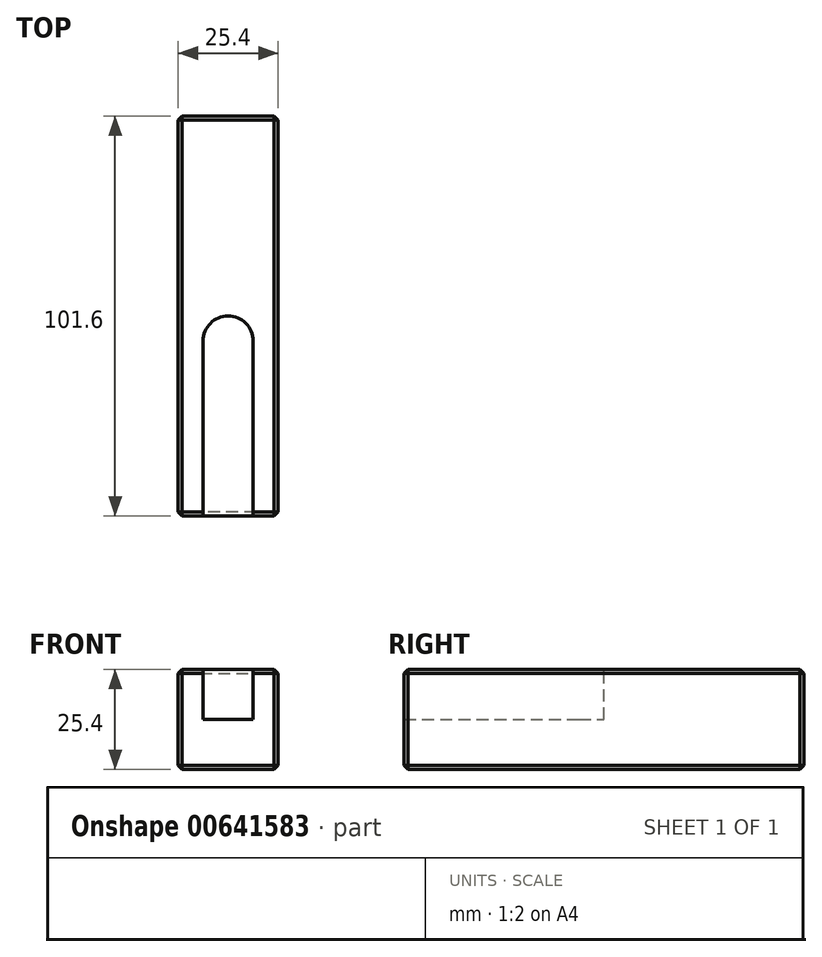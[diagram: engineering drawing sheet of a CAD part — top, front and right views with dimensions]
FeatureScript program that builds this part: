
annotation { "Feature Type Name" : "Feature", "Feature Type Description" : "" }
export const myFeature = defineFeature(function(context is Context, id is Id, definition is map)
    precondition{}
    {
        {
            var Q0;
            Q0=qCreatedBy(makeId("Front.planeOp"),FACE);
            var sketch = newSketch(context, id + "F0", { "sketchPlane" : qUnion([Q0])});
            skLineSegment(sketch, "E0.bottom", {"start": v(12.7, -12.7) * mm, "end": v(-12.7, -12.7) * mm});
            skLineSegment(sketch, "E0.top", {"start": v(12.7, 12.7) * mm, "end": v(-12.7, 12.7) * mm});
            skLineSegment(sketch, "E0.left", {"start": v(12.7, -12.7) * mm, "end": v(12.7, 12.7) * mm});
            skLineSegment(sketch, "E0.right", {"start": v(-12.7, -12.7) * mm, "end": v(-12.7, 12.7) * mm});
            skPoint(sketch, "E0.middle", {"position": v(0, 0) * mm});
            skSolve(sketch);
        }
        {
            var Q0;
            Q0=makeQuery(id+"F0.imprint","IMPRINT",FACE,{"disambiguationData":[TD([[makeQuery(id+"F0.imprint","IMPRINT",EDGE,{"derivedFrom":sQuery(id+"F0.wireOp",EDGE,"E0.bottom")}),-1.0]])]});
            extrude(context, id + "F1", {"entities" : qUnion([Q0]), "endBound" : BoundingType.SYMMETRIC, "oppositeDirection" : true, "depth" : (25.4 * 4) * mm, "offsetDistance" : 25 * mm});
        }
        {
            var Q0;
            Q0=makeQuery(id+"F1.opExtrude","SWEPT_FACE",FACE,{"disambiguationData":[OSD([sQuery(id+"F0.wireOp",EDGE,"E0.top")])]});
            var sketch = newSketch(context, id + "F2", { "sketchPlane" : qUnion([Q0])});
            skLineSegment(sketch, "E1.bottom", {"start": v(-6.35, -50.8) * mm, "end": v(6.35, -50.8) * mm});
            skLineSegment(sketch, "E1.left", {"start": v(-6.35, -50.8) * mm, "end": v(-6.35, -6.35) * mm});
            skLineSegment(sketch, "E1.right", {"start": v(6.35, -50.8) * mm, "end": v(6.35, -6.35) * mm});
            skArc(sketch, "E2", {"start": v(6.35, -6.35) * mm, "mid": v(0, 0) * mm, "end": v(-6.35, -6.35) * mm});
            skSolve(sketch);
        }
        {
            var Q0;
            Q0=makeQuery(id+"F2.imprint","IMPRINT",FACE,{"disambiguationData":[TD([[makeQuery(id+"F2.imprint","IMPRINT",EDGE,{"derivedFrom":sQuery(id+"F2.wireOp",EDGE,"E1.bottom")}),-1.0]])]});
            extrude(context, id + "F3", {"entities" : qUnion([Q0]), "operationType" : NewBodyOperationType.REMOVE, "oppositeDirection" : true, "depth" : (25.4 / 2) * mm, "offsetDistance" : 25 * mm});
        }
        {
            var Q0;
            Q0=makeQuery(id+"F1.opExtrude","SWEPT_EDGE",EDGE,{"disambiguationData":[OSD([sQuery(id+"F0.wireOp",EDGE,"E0.top"),sQuery(id+"F0.wireOp",EDGE,"E0.left")])]});
            var Q1;
            Q1=makeQuery(id+"F1.opExtrude","CAP_EDGE",EDGE,{"disambiguationData":[OSD([sQuery(id+"F0.wireOp",EDGE,"E0.left")])],"isStart":false});
            var Q2;
            Q2=makeQuery(id+"F1.opExtrude","SWEPT_EDGE",EDGE,{"disambiguationData":[OSD([sQuery(id+"F0.wireOp",EDGE,"E0.bottom"),sQuery(id+"F0.wireOp",EDGE,"E0.left")])]});
            var Q3;
            Q3=makeQuery(id+"F1.opExtrude","CAP_EDGE",EDGE,{"disambiguationData":[OSD([sQuery(id+"F0.wireOp",EDGE,"E0.left")])],"isStart":true});
            var Q4;
            Q4=makeQuery(id+"F1.opExtrude","CAP_EDGE",EDGE,{"disambiguationData":[OSD([sQuery(id+"F0.wireOp",EDGE,"E0.bottom")])],"isStart":true});
            var Q5;
            {var subQ0=sQuery(id+"F0.wireOp",EDGE,"E0.left");var subQ1=sQuery(id+"F0.wireOp",EDGE,"E0.top");Q5=makeQuery(id+"F3.boolean.opBoolean","SPLIT",EDGE,{"disambiguationData":[TD([makeQuery(id+"F1.opExtrude","SWEPT_FACE",FACE,{"disambiguationData":[OSD([subQ0])]})])],"derivedFrom":makeQuery(id+"F1.opExtrude","CAP_EDGE",EDGE,{"disambiguationData":[OSD([subQ1])],"isStart":true})});}
            var Q6;
            {var subQ0=sQuery(id+"F0.wireOp",EDGE,"E0.right");var subQ1=sQuery(id+"F0.wireOp",EDGE,"E0.top");Q6=makeQuery(id+"F3.boolean.opBoolean","SPLIT",EDGE,{"disambiguationData":[TD([makeQuery(id+"F1.opExtrude","SWEPT_FACE",FACE,{"disambiguationData":[OSD([subQ0])]})])],"derivedFrom":makeQuery(id+"F1.opExtrude","CAP_EDGE",EDGE,{"disambiguationData":[OSD([subQ1])],"isStart":true})});}
            var Q7;
            Q7=makeQuery(id+"F1.opExtrude","CAP_EDGE",EDGE,{"disambiguationData":[OSD([sQuery(id+"F0.wireOp",EDGE,"E0.right")])],"isStart":true});
            var Q8;
            Q8=makeQuery(id+"F1.opExtrude","SWEPT_EDGE",EDGE,{"disambiguationData":[OSD([sQuery(id+"F0.wireOp",EDGE,"E0.top"),sQuery(id+"F0.wireOp",EDGE,"E0.right")])]});
            var Q9;
            Q9=makeQuery(id+"F1.opExtrude","CAP_EDGE",EDGE,{"disambiguationData":[OSD([sQuery(id+"F0.wireOp",EDGE,"E0.top")])],"isStart":false});
            var Q10;
            Q10=makeQuery(id+"F1.opExtrude","SWEPT_EDGE",EDGE,{"disambiguationData":[OSD([sQuery(id+"F0.wireOp",EDGE,"E0.bottom"),sQuery(id+"F0.wireOp",EDGE,"E0.right")])]});
            var Q11;
            Q11=makeQuery(id+"F1.opExtrude","CAP_EDGE",EDGE,{"disambiguationData":[OSD([sQuery(id+"F0.wireOp",EDGE,"E0.right")])],"isStart":false});
            var Q12;
            Q12=makeQuery(id+"F1.opExtrude","CAP_EDGE",EDGE,{"disambiguationData":[OSD([sQuery(id+"F0.wireOp",EDGE,"E0.bottom")])],"isStart":false});
            chamfer(context, id + "F4", {"entities" : qUnion([Q0, Q1, Q2, Q3, Q4, Q5, Q6, Q7, Q8, Q9, Q10, Q11, Q12]), "width" : 1 * mm, "tangentPropagation" : true});
        }
    });
